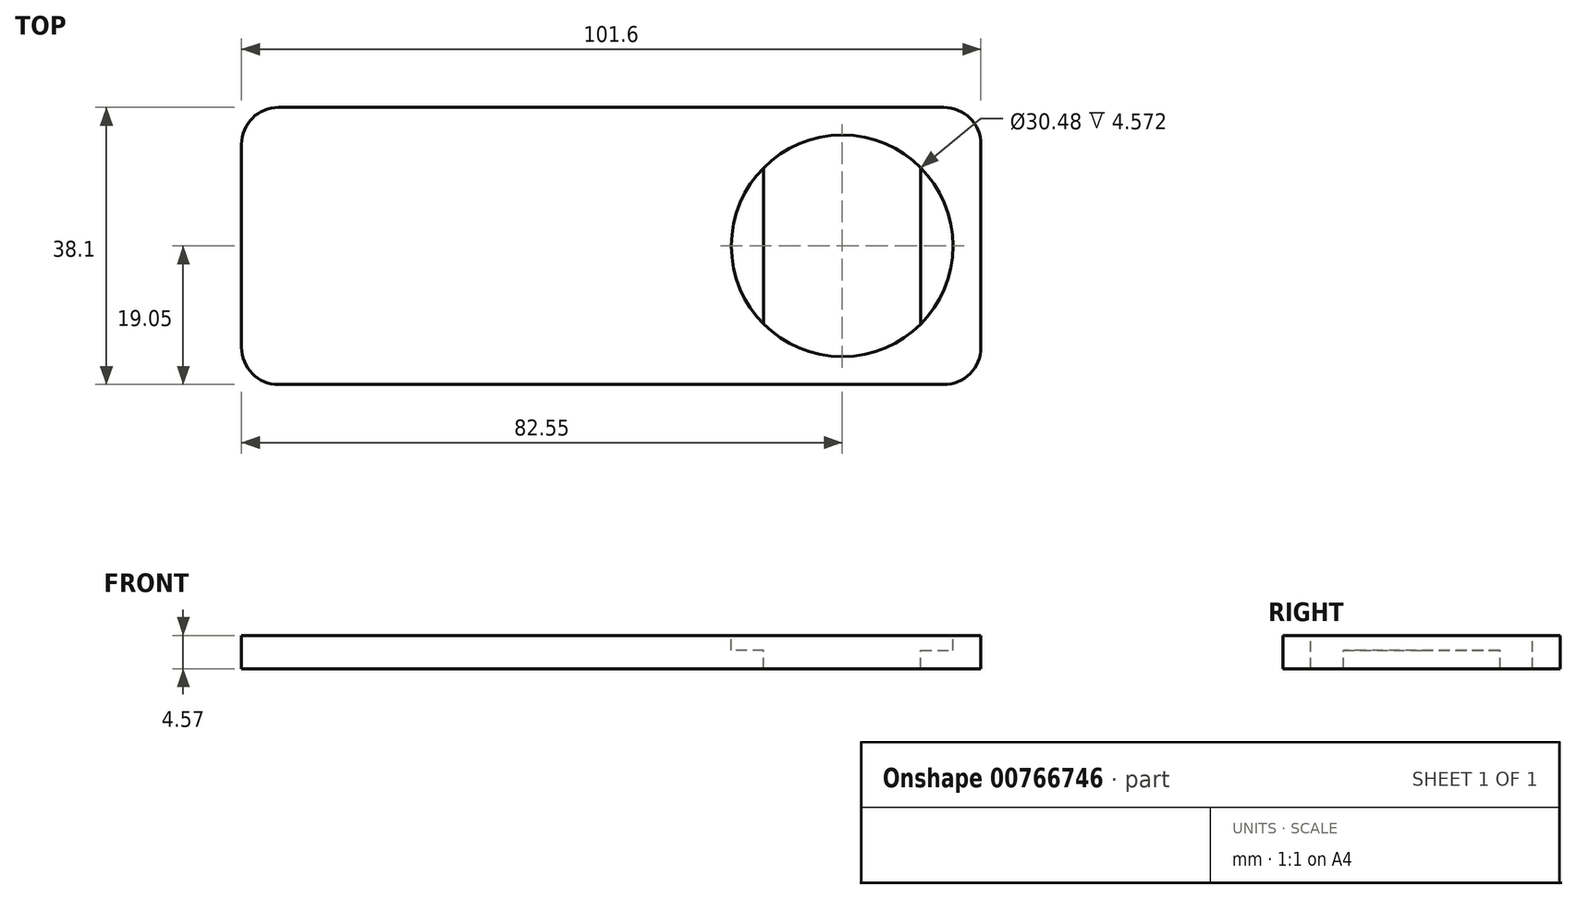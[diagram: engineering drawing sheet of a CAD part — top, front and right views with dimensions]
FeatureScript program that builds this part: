
annotation { "Feature Type Name" : "Feature", "Feature Type Description" : "" }
export const myFeature = defineFeature(function(context is Context, id is Id, definition is map)
    precondition{}
    {
        {
            var Q0;
            Q0=qCreatedBy(makeId("Front.planeOp"),FACE);
            var sketch = newSketch(context, id + "F0", { "sketchPlane" : qUnion([Q0])});
            skLineSegment(sketch, "E0.bottom", {"start": v(-75.42, -12.49) * mm, "end": v(26.18, -12.49) * mm});
            skLineSegment(sketch, "E0.top", {"start": v(-75.42, -17.06) * mm, "end": v(26.18, -17.06) * mm});
            skLineSegment(sketch, "E0.left", {"start": v(-75.42, -12.49) * mm, "end": v(-75.42, -17.06) * mm});
            skLineSegment(sketch, "E0.right", {"start": v(26.18, -12.49) * mm, "end": v(26.18, -17.06) * mm});
            skSolve(sketch);
        }
        {
            var Q0;
            Q0=makeQuery(id+"F0.imprint","IMPRINT",FACE,{"disambiguationData":[TD([[makeQuery(id+"F0.imprint","IMPRINT",EDGE,{"derivedFrom":sQuery(id+"F0.wireOp",EDGE,"E0.bottom")}),-1.0]])]});
            extrude(context, id + "F1", {"entities" : qUnion([Q0]), "depth" : 38.1 * mm, "offsetDistance" : 25.4 * mm});
        }
        {
            var Q0;
            Q0=makeQuery(id+"F1.opExtrude","CAP_EDGE",EDGE,{"disambiguationData":[OSD([sQuery(id+"F0.wireOp",EDGE,"E0.right")])],"isStart":false});
            var Q1;
            Q1=makeQuery(id+"F1.opExtrude","CAP_EDGE",EDGE,{"disambiguationData":[OSD([sQuery(id+"F0.wireOp",EDGE,"E0.right")])],"isStart":true});
            var Q2;
            Q2=makeQuery(id+"F1.opExtrude","CAP_EDGE",EDGE,{"disambiguationData":[OSD([sQuery(id+"F0.wireOp",EDGE,"E0.left")])],"isStart":false});
            var Q3;
            Q3=makeQuery(id+"F1.opExtrude","CAP_EDGE",EDGE,{"disambiguationData":[OSD([sQuery(id+"F0.wireOp",EDGE,"E0.left")])],"isStart":true});
            fillet(context, id + "F2", {"entities" : qUnion([Q0, Q1, Q2, Q3]), "radius" : 5.08 * mm, "tangentPropagation" : true, "allowEdgeOverflow" : false});
        }
        {
            var Q0;
            Q0=makeQuery(id+"F1.opExtrude","SWEPT_FACE",FACE,{"disambiguationData":[OSD([sQuery(id+"F0.wireOp",EDGE,"E0.bottom")])]});
            var sketch = newSketch(context, id + "F3", { "sketchPlane" : qUnion([Q0])});
            skPoint(sketch, "E1", {"position": v(7.13, -19.05) * mm});
            skSolve(sketch);
        }
        {
            var Q0;
            Q0=sQuery(id+"F3.wireOp",VERTEX,"E1");
            var Q1;
            Q1=makeQuery(id+"F1.opExtrude","SWEPT_BODY",BODY,{"disambiguationData":[OSD([sQuery(id+"F0.wireOp",EDGE,"E0.bottom"),sQuery(id+"F0.wireOp",EDGE,"E0.top"),sQuery(id+"F0.wireOp",EDGE,"E0.left"),sQuery(id+"F0.wireOp",EDGE,"E0.right")])]});
            hole(context, id + "F4", {"style" : HoleStyle.SIMPLE, "endStyle" : HoleEndStyle.THROUGH, "holeDiameter" : 30.48 * mm, "majorDiameter" : 6.35 * mm, "isTappedThrough" : true, "tappedDepth" : 12.7 * mm, "tapClearance" : 3, "locations" : qUnion([Q0]), "scope" : qUnion([Q1])});
        }
        {
            var Q0;
            Q0=makeQuery(id+"F1.opExtrude","SWEPT_FACE",FACE,{"disambiguationData":[OSD([sQuery(id+"F0.wireOp",EDGE,"E0.bottom")])]});
            var sketch = newSketch(context, id + "F5", { "sketchPlane" : qUnion([Q0])});
            skLineSegment(sketch, "E2", {"start": v(-3.66, -8.29) * mm, "end": v(-3.66, -29.81) * mm});
            skLineSegment(sketch, "E3", {"start": v(17.93, -8.3) * mm, "end": v(17.93, -29.8) * mm});
            skSolve(sketch);
        }
        {
            var Q0;
            {var subQ0=sQuery(id+"F5.wireOp",EDGE,"E3");Q0=makeQuery(id+"F5.imprint","IMPRINT",FACE,{"disambiguationData":[TD([[makeQuery(id+"F5.imprint","IMPRINT",EDGE,{"derivedFrom":subQ0}),1.0]])]});}
            var Q1;
            {var subQ0=sQuery(id+"F5.wireOp",EDGE,"E2");Q1=makeQuery(id+"F5.imprint","IMPRINT",FACE,{"disambiguationData":[TD([[makeQuery(id+"F5.imprint","IMPRINT",EDGE,{"derivedFrom":subQ0}),-1.0]])]});}
            var Q2;
            Q2=sQuery(id+"F5.wireOp",EDGE,"E3");
            extrude(context, id + "F6", {"entities" : qUnion([Q0, Q1]), "operationType" : NewBodyOperationType.ADD, "surfaceEntities" : qUnion([Q2]), "oppositeDirection" : true, "depth" : 4.57 * mm, "offsetDistance" : 25.4 * mm, "hasSecondDirection" : true, "secondDirectionOppositeDirection" : true, "secondDirectionDepth" : 2.03 * mm});
        }
    });
